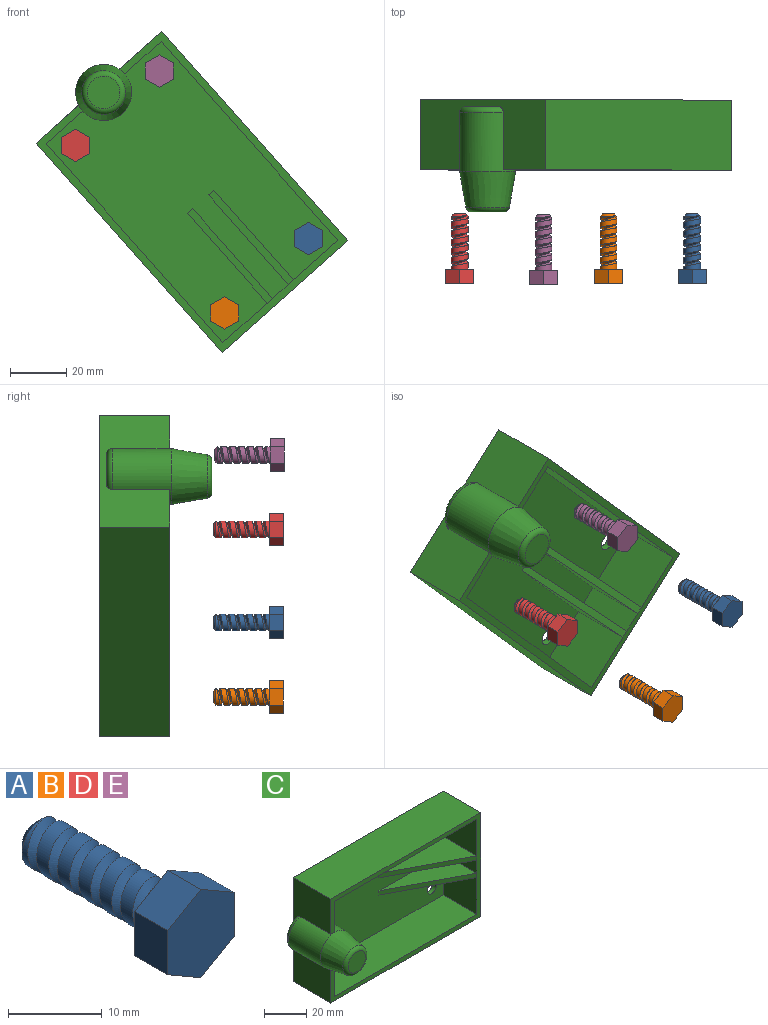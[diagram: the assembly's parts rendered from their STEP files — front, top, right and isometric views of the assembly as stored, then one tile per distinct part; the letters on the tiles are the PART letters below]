
ASSEMBLY  parts=5 mates=4
PART A: 16 faces, bbox 10.1x25.1x11.6 mm
  f0: cylinder r=3mm len=19mm, axis (0,-1,0), area 208.9mm2, adj f1,f9,f12,f13,f14,f15
  f1: cone r=3mm half-angle=45deg, axis (0,-1,0), area 21.1mm2, adj f0,f10,f14,f15
  f2: plane 5x5mm, normal (0.5,0,-0.87), area 28.9mm2, adj f3,f7,f8,f9
  f3: plane 5.77x5mm, normal (1,0,0), area 28.9mm2, adj f2,f4,f8,f9
  f4: plane 5x5mm, normal (0.5,0,0.87), area 28.9mm2, adj f3,f5,f8,f9
  f5: plane 5x5mm, normal (-0.5,0,0.87), area 28.9mm2, adj f4,f6,f8,f9
  f6: plane 5.77x5mm, normal (-1,0,0), area 28.9mm2, adj f5,f7,f8,f9
  f7: plane 5x5mm, normal (-0.5,0,-0.87), area 28.9mm2, adj f2,f6,f8,f9
  f8: plane 11.55x10mm, normal (0,-1,0), area 86.6mm2, adj f2,f3,f4,f5,f6,f7
  f9: plane 11.62x10.08mm, normal (0,1,0), area 55.2mm2, adj f0,f2,f3,f4,f5,f6,f7,f11
  f10: plane 4x4mm, normal (0,1,0), area 12.6mm2, adj f1
  f11: cylinder r=3.58mm len=4.99mm, axis (0,-1,0), area 3.5mm2, adj f9,f12,f13
  f12: plane 1.73x1.67mm, normal (0,0,-1), area 1.3mm2, adj f0,f9,f11,f13,f15
  f13: bspline ~20x8.26mm, area 127.4mm2, adj f0,f9,f11,f12,f14,f15
  f14: plane 1.15x1.09mm, normal (0,0,1), area 0.6mm2, adj f0,f1,f13,f15
  f15: bspline ~20x8.26mm, area 122.9mm2, adj f0,f1,f12,f13,f14
PART B: same geometry as A
PART C: 30 faces, bbox 108.3x40x60 mm
  f0: plane 95x55mm, normal (0,-1,0), area 4741.1mm2, adj f2,f3,f4,f5,f11,f12,f13,f14
  f1: plane 60x25mm, normal (-1,0,0), area 1066.1mm2, adj f6,f7,f9,f10,f24,f25,f29
  f2: plane 22.5x17.5mm, normal (1,0,0), area 393.8mm2, adj f0,f6,f13,f24
  f3: plane 22.5x17.5mm, normal (1,0,0), area 393.8mm2, adj f0,f6,f11,f24
  f4: plane 22.5x21.25mm, normal (-1,0,0), area 478.1mm2, adj f0,f6,f11,f17
  f5: plane 22.5x7.5mm, normal (-1,0,0), area 168.7mm2, adj f0,f6,f14,f18
  f6: plane 100x60mm, normal (0,-1,0), area 725.5mm2, adj f1,f2,f3,f4,f5,f7,f8,f9
  f7: plane 100x25mm, normal (0,0,-1), area 2500mm2, adj f1,f6,f8,f10
  f8: plane 60x25mm, normal (1,0,0), area 1500mm2, adj f6,f7,f9,f10
  f9: plane 100x25mm, normal (0,0,1), area 2500mm2, adj f1,f6,f8,f10
  f10: plane 100x60mm, normal (0,1,0), area 5886.9mm2, adj f1,f7,f8,f9,f20,f21,f22,f23
  f11: plane 95x22.5mm, normal (0,0,1), area 2137.5mm2, adj f0,f3,f4,f6
  f12: plane 22.5x21.25mm, normal (-1,0,0), area 478.1mm2, adj f0,f6,f13,f15
  f13: plane 95x22.5mm, normal (0,0,-1), area 2137.5mm2, adj f0,f2,f6,f12
  f14: plane 42.75x22.5mm, normal (0,0,-1), area 480.9mm2, adj f0,f5,f16
  f15: plane 42.75x22.5mm, normal (0,0,1), area 480.9mm2, adj f0,f12,f16
  f16: plane 42.75x22.5mm, normal (-0.47,-0.88,0), area 120.8mm2, adj f0,f6,f14,f15
  f17: plane 42.75x22.5mm, normal (0,0,-1), area 480.9mm2, adj f0,f4,f19
  f18: plane 42.75x22.5mm, normal (0,0,1), area 480.9mm2, adj f0,f5,f19
  f19: plane 42.75x22.5mm, normal (-0.47,-0.88,0), area 120.8mm2, adj f0,f6,f17,f18
  f20: cylinder r=3mm len=6mm, axis (0,-1,0), area 47.1mm2, adj f0,f10
  f21: cylinder r=3mm len=6mm, axis (0,-1,0), area 47.1mm2, adj f0,f10
  f22: cylinder r=3mm len=6mm, axis (0,-1,0), area 47.1mm2, adj f0,f10
  f23: cylinder r=3mm len=6mm, axis (0,-1,0), area 47.1mm2, adj f0,f10
  f24: cylinder r=10mm len=23mm, axis (0,1,0), area 1278.7mm2, adj f0,f1,f2,f3,f6,f27,f29
  f25: plane 15.2x5.5mm, normal (0,1,0), area 61.2mm2, adj f1,f29
  f26: plane 11.63x11.63mm, normal (0,-1,0), area 106.2mm2, adj f28
  f27: cone r=10mm half-angle=9.8deg, axis (0,1,0), area 728mm2, adj f24,f28
  f28: torus R=5.82mm, axis (0,-1,0), area 123.2mm2, adj f26,f27
  f29: torus R=8mm, axis (0,-1,0), area 75.6mm2, adj f1,f24,f25
PART D: same geometry as A
PART E: same geometry as A
PLACE A t=(-33.67,-27.39,-137.1)mm
PLACE B t=(-63.58,-27.39,-163.66)mm
PLACE C rot(axis=(0,1,0),48.4deg) t=(-75.19,33.09,-120.47)mm
PLACE D t=(-116.7,-27.39,-103.85)mm
PLACE E t=(-86.8,-27.77,-77.28)mm
MATE cylindrical B.f0 <-> C.f22  axis (0,1,0) through (-63.58,-7.39,-163.66)mm
MATE cylindrical E.f0 <-> C.f20  axis (0,1,0) through (-86.8,-7.77,-77.28)mm
MATE cylindrical A.f0 <-> C.f21  axis (0,1,0) through (-33.67,-7.39,-137.1)mm
MATE cylindrical D.f0 <-> C.f23  axis (0,1,0) through (-116.7,-7.39,-103.85)mm
